# Revit family: 1702a_ACAK
name_source: partatom
category: Communication Devices
units: mm (PartAtom-declared; Revit-internal decimal feet)

## family parameters
Cut with Voids When Loaded = No
Host = Face
Maintain Annotation Orientation = No
OmniClass Number = 23.85.80.11.27
OmniClass Title = Lighting Controls
Part Type = Normal
Room Calculation Point = No
Round Connector Dimension = Use Diameter
Shared = Yes

## types (1)
- 1702a_ACAK
    Assembly Code = D5090
    Certifications = UL and cUL listed
    Default Elevation = 48 "
    Description = For ceiling and wall mount sensors used with acoustic ceiling tile. ACAK uses integral cutting teeth for quicker installation.
    Height = 6.5 "
    Housing Material = Paint - Matte White
    Manufacturer = NX Lighting Controls
    Model = ACAK — Acoustic Ceiling Mounting Kit
    Type Comments = ACAK — Acoustic Ceiling Mounting Kit
    URL = https://www.currentlighting.com
    Warranty = 5-Years Warranty
    Width = 6.5 "

## geometry (parser evidence)
native form markers: Sweep x3
no freeform markers — native parametric forms only
